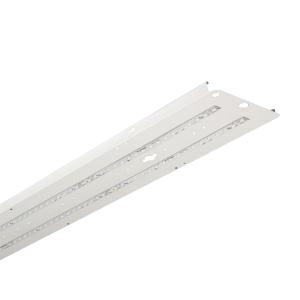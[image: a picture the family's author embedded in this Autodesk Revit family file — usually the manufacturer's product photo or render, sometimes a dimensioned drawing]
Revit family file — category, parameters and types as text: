
# Revit family: 3f_filippi_-_kit_led_retrofit_per_schermo_in_vetro_3f_filippi_-_a5104_a5184_-_kit_led_i3f_76__a3f_91__a3_0125028f5d10ea62
name_source: partatom
category: Lighting Fixtures
units: mm (PartAtom-declared; Revit-internal decimal feet)

## family parameters
Cut with Voids When Loaded = No
Host = Face
Light Source = No
Part Type = Normal
Room Calculation Point = No
Round Connector Dimension = Use Diameter
Shared = No

## types (1)
- 3F Filippi - Kit LED Retrofit per schermo in vetro (1 x LED, 6922 lm, 49 W, 4000 K)
    Apparent Load = 49 VA
    Approval mark = ENEC
    CIE Flux Codes = 59 90 99 100 100
    Color Rendering = 80
    Color Temperature = 4000 K
    Control Gear = Electronic ballast
    Default Elevation = 1800 mm
    Description = Led retrofit kit suitable for Fluorescent Beta 2x i3F 76, A3F 91 and A3F 93 luminaires.

ILLUMINOTECHNICAL
Luminous efficiency 100% (DLOR 97%, ULOR 3%).
Initial luminous flux of the luminaire 6922 lm.
Symmetric concentrated distribution.
Installation Interdistance Transv.D = 0.98 x hu - Long.D = 1.24 x hu.
Tabular UGR (CIE 117 - 4H-8H; S=0.25H; 70/50/20): RUG 18.5 - 21.1.
Beam angle: 84° - 101°.
Luminous efficacy 141 lm/W.
Lifetime (L93/B10): 30000 h. (tq+25°C)
Lifetime (L90/B10): 50000 h. (tq+25°C)
Lifetime (L85/B10): 80000 h. (tq+25°C)
Lifetime (L80/B10): 100000 h. (tq+25°C)
Lifetime (L85/B10): 50000 h. (tq+35°C)
Sudden decreased luminous flux after 50000 hours: 0% (C0).
Photobiological safety in compliance with IEC/TR 62778: RG0 risk exempt, (IEC 62471).
In compliance with IEC/EN 62722-2-1 - IEC/EN 62717 standards.

SOURCE
2 linear LED modules 22W/840.
Energy efficiency class (UE 2019/2020 - UE 2019/2015): D.
CIE 13.3 Colour rendering index: CRI >80 (R9 <50%).
IES TM-30 Fidelity Index: Rf = 84 Rg = 95.
CCT nominal colour temperature 4000 K.
Colour initial tolerance (MacAdam): SDCM 3.

MECHANICAL
Gear-tray unit in hot-galvanised steel, painted in white polyester, fixed to the housing by means of "Ribloc" rapid devices in galvanised steel, hinged opening.
Luminaire with limited surface temperature. - D - (EN 60598-2-24)
Dimensions: 1565x235 mm, height 135 mm. Weight 6.627 kg.
Glow-wire test resistance 850°C.

ELECTRICAL
Halogen Free electronic wiring 230V-50/60Hz, power factor 0.97, THD <25%, constant output current, SELV, class I, 1 driver.
Power of the luminaire 49 W.
CE - IEC 60598-1 - EN 60598-1.
SAFE FLICKER: PstLM=<1 and SVM=<0.4 (IEC TR 61547-1 and IEC TR 63158), to ensure a more comfortable and safe light.
Luminaire compliant with EN 60598-2-22 for power supply from a centralised emergency system CPSS (Central Power Supply System), not incorporated in the luminaire - high risk areas excluded. The default power and flux are 100% in AC and 100% in DC.
Ambient temperature from -20°C to +35°C.
Temperature class T6 max 85°C.
Relative humidity UR: <85%.

INSTALLATION
Retrofit.
Correct installation of the retrofit LED kit, compliant with EN 60598-1 and CE marked, inside the 3F Filippi - Beta 2x i3F 76, A3F 91 and A3F 93 Fluorescent luminaires must be only carried out by qualified personnel to ensure compliance with the national installation standards.
Attention: to maintain the degree of protection of the device and for the purposes of validity of the guarantee of the new retrofit kits, it is imperative to replace the old cable guides (on the body of the device) with the new ones supplied.
All accessories dedicated to this product are available on the Catalog and on our website www.3F-Filippi.com.

ACCESSORIES
A5184 - Printed glass Beta 2x i3F 76 - L1565.

WARNING
Fixture not suitable for cold stores with an ambient temperature <0°C and/or relative humidity >85%.
Luminaire designed for disposal/recycling at end-of-life.
Replaceable (LED only) light source by a professional. Replaceable control gear by a professional.
    Height = 135 mm
    Lamp = 1 x LED
    Lamp Light Flux = 6922 lm
    Lamp Power = 49 W
    Lamp count = 1
    Length = 1565 mm
    Lifetime = 50000 h
    Luminous efficacy = 141 lm/W
    Manufacturer = 3F Filippi
    ModVariant = No
    Model = 3F Filippi - A5104+A5184 - Kit LED I3F 76, A3F 91, A3F 93-L1565-2X22W CONC + VS
    Mounting Place = Ceiling
    Mounting Type = Surface mounted
    Number of Poles = 1
    OnlyDefault = Yes
    Power Factor = 1
    Product Name = 3F Filippi - Kit LED Retrofit per schermo in vetro
    Product group = ceiling mounted luminaire
    ProductGroupID = 3
    Protection Class = Protection class I
    Protection Degree = Degree of protection
    RLX_Detail_Level = 1
    RLX_Emergency_Light_Flux = 0 lm
    RLX_Emergency_Type = 0
    RLX_Emergency_Type_DB = No
    RlxData = <blob elided: 53477 chars, md5=ea359002>
    Socket = socket
    Standby Power = 0 W
    System Light Flux = 6922 lm
    System Power = 49 W
    Type Comments = Product without accessories
    Type Image = 3ffilippi_a5104_a5184.jpg
    URL = http://relux.com
    VarID = ---
    Voltage = 0 V
    Weight = 0.00 kg
    Width = 235 mm

## geometry (parser evidence)
native form markers: Blend x4, Sweep x11
no freeform markers — native parametric forms only
